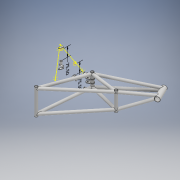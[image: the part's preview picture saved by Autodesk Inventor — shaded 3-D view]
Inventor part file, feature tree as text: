
AUTODESK INVENTOR PART (.ipt)
format: ipt  version: 2018 (Build 220112000, 112)  size: 1,001,472 bytes
history: native  units: mm
features: other x12, sketch x3, plane x2, surface_op x2, extrude x1, mirror x1, boolean_combine x1, delete_face x1
ambient origin geometry x8: Origin, YZ Plane, XZ Plane, XY Plane, X Axis, Y Axis, Z Axis, Center Point
bodies: Solid14 (feature_tree), Solid8 (feature_tree), Solid16 (feature_tree), Solid17 (feature_tree), Solid18 (feature_tree), Solid1 (feature_tree)
feature tree (23):
  other  "SeatMount.ipt"
  other  "Annotations"
  plane  "Work Plane1"
  extrude  "Extrusion1"  Depth=10.0mm
  mirror  "Mirror1"
  boolean_combine  "Combine1"
  delete_face  "Delete Face1"
  plane  "Work Plane2"
  sketch  "Sketch2"  dims[d2=40.0mm d3=40.0mm d4=40.0mm d5=40.0mm d6=47.75mm d7=0.0mm d8=0.0mm d9=0.0mm d10=0.0mm d11=0.0mm d14=14.5mm d15=1.0mm d16=3.0mm d17=1.0mm d18=3.0mm d21=75.501655mm d22=75.501415mm]
  surface_op  "Trim1"
  surface_op  "Trim2"
  other  "Solid8::SeatMount.ipt"
  other  "TaggingFeature1"
  sketch  "3D Sketch3"
  sketch  "Sketch1"  dims[d0=10.0mm d1=37.75mm]
  other  "Solid1::SeatMount.ipt"
  other  "PlateA::SeatMount.ipt"
  other  "PlateB::SeatMount.ipt"
  other  "Solid3::SeatMount.ipt"
  other  "OffsetSrf1"
  other  "OffsetSrf2"
  other  "Linear Dimension 1"
  other  "Linear Dimension 2"
